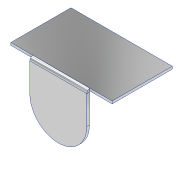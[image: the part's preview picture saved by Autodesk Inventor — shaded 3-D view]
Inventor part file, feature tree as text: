
AUTODESK INVENTOR PART (.ipt)
format: ipt  version: 2022 (Build 260153000, 153)  size: 201,216 bytes
history: native  units: mm
features: sketch x8, extrude x5, sheet_metal_op x2, hole x2, thicken_offset x1, fillet x1, plane x1, mirror x1, other x1, projected_geometry x1
ambient origin geometry x8: Origin, YZ Plane, XZ Plane, XY Plane, X Axis, Y Axis, Z Axis, Center Point
bodies: Solid1 (feature_tree)
feature tree (23):
  extrude  "Extrusion1"  Depth=6.5mm
  sheet_metal_op  "Face1"
  extrude  "Extrusion3"  Depth=45.0mm
  hole  "Hole1"  [1 undecoded]
  hole  "Hole2"  [1 undecoded]
  extrude  "Extrusion2"  Depth=2.0mm
  thicken_offset  "Thicken2"
  fillet  "Fillet2"  Radius=31.0mm
  plane  "Work Plane1"
  extrude  "Extrusion4"  Depth=2.0mm
  extrude  "Extrusion5"  Depth=10.0mm
  mirror  "Mirror2"
  sketch  "Sketch1"  dims[d1=37.0mm d3=6.5mm]
  sketch  "Sketch2"  dims[d4=50.0mm d5=45.0mm]
  other  "Plate1"
  sheet_metal_op  "Bend1"
  sketch  "Sketch3"  dims[d6=2.0mm d7=0.0mm d8=2.0mm]
  sketch  "Sketch4"  dims[d9=0.5mm d10=2.0mm d11=1.0mm]
  sketch  "Sketch6"  dims[d12=4.0mm d13=2.0mm d14=31.0mm]
  sketch  "Sketch8"  dims[d15=30.0mm d17=360.0deg]
  sketch  "Sketch10"  dims[d19=3.4mm d20=6.0mm d21=4.0mm d22=2.0mm d23=90.0deg d24=2.0mm d25=20.594885mm]
  sketch  "Sketch12"  dims[d26=34.0mm d27=69.0mm d28=3.4mm d29=6.0mm d30=4.0mm d31=2.0mm d32=90.0deg d33=8.0mm d34=20.594885mm d36=7.0mm d45=25.0mm d46=2.0mm d47=0.0mm d48=0.0mm d50=80.0mm d51=10.0mm d52=0.0mm d53=3.0mm d56=1.0mm d57=1.0mm d66=-18.0mm d69=38.0mm d70=5.0mm d71=0.0mm d72=12.0mm d73=14.0mm d74=3.0mm d75=0.0mm]
  projected_geometry  "Project Cut Edges1"
note: 2 required parameter values undecoded (feature->parameter linkage not recoverable at this tier; creation-order binding heuristic only, values carry confidence <= 0.55)
